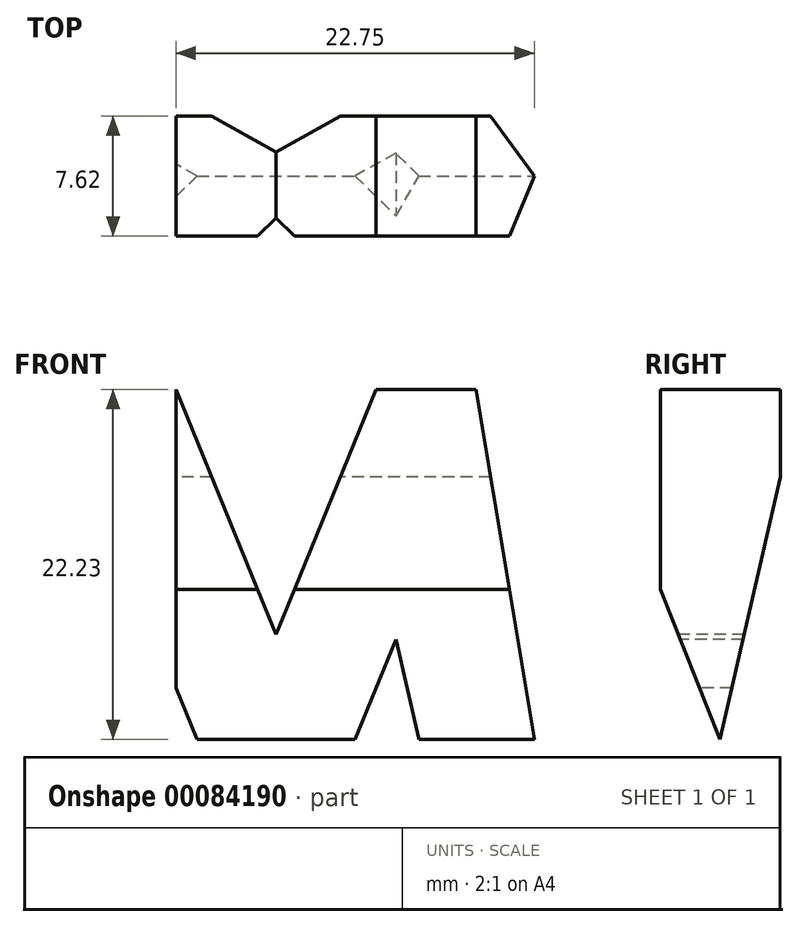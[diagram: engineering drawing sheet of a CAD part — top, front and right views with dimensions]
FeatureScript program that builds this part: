
annotation { "Feature Type Name" : "Feature", "Feature Type Description" : "" }
export const myFeature = defineFeature(function(context is Context, id is Id, definition is map)
    precondition{}
    {
        {
            var Q0;
            Q0=qCreatedBy(makeId("Front.planeOp"),FACE);
            var sketch = newSketch(context, id + "F0", { "sketchPlane" : qUnion([Q0])});
            skLineSegment(sketch, "E0", {"start": v(0, 0) * mm, "end": v(0, 38.1) * mm});
            skLineSegment(sketch, "E1", {"start": v(0, 38.1) * mm, "end": v(38.1, 38.1) * mm});
            skLineSegment(sketch, "E2", {"start": v(38.1, 38.1) * mm, "end": v(38.1, 0) * mm});
            skLineSegment(sketch, "E3", {"start": v(0, 0) * mm, "end": v(38.1, 0) * mm});
            skSolve(sketch);
        }
        {
            var Q0;
            Q0=makeQuery(id+"F0.imprint","IMPRINT",FACE,{"disambiguationData":[TD([[makeQuery(id+"F0.imprint","IMPRINT",EDGE,{"derivedFrom":sQuery(id+"F0.wireOp",EDGE,"E0")}),-1.0]])]});
            extrude(context, id + "F1", {"entities" : qUnion([Q0]), "depth" : 38.1 * mm});
        }
        {
            var Q0;
            Q0=qCreatedBy(makeId("Front.planeOp"),FACE);
            cPlane(context, id + "F2", {"entities" : qUnion([Q0]), "cplaneType" : CPlaneType.OFFSET, "offset" : 38.1 * mm, "width" : 152.4 * mm, "height" : 152.4 * mm});
        }
        {
            var Q0;
            Q0=qCreatedBy(makeId("Right.planeOp"),FACE);
            cPlane(context, id + "F3", {"entities" : qUnion([Q0]), "cplaneType" : CPlaneType.OFFSET, "offset" : 38.1 * mm, "width" : 152.4 * mm, "height" : 152.4 * mm});
        }
        {
            var Q0;
            Q0=qCreatedBy(makeId("Top.planeOp"),FACE);
            cPlane(context, id + "F4", {"entities" : qUnion([Q0]), "cplaneType" : CPlaneType.OFFSET, "offset" : 38.1 * mm, "width" : 152.4 * mm, "height" : 152.4 * mm});
        }
        {
            var Q0;
            Q0=qCreatedBy(id+"F3.planeOp",FACE);
            var sketch = newSketch(context, id + "F5", { "sketchPlane" : qUnion([Q0])});
            skLineSegment(sketch, "E4", {"start": v(0, 0) * mm, "end": v(-38.1, 0) * mm});
            skLineSegment(sketch, "E5", {"start": v(-38.1, 0) * mm, "end": v(-38.1, 38.1) * mm});
            skLineSegment(sketch, "E6", {"start": v(-38.1, 38.1) * mm, "end": v(0, 38.1) * mm});
            skLineSegment(sketch, "E7", {"start": v(0, 38.1) * mm, "end": v(0, -1.8) * mm});
            skLineSegment(sketch, "E8", {"start": v(-38.1, 38.1) * mm, "end": v(-31.75, 0) * mm});
            skLineSegment(sketch, "E9", {"start": v(-31.75, 0) * mm, "end": v(-25.4, 0) * mm});
            skLineSegment(sketch, "E10", {"start": v(-25.4, 0) * mm, "end": v(-19.05, 15.88) * mm});
            skLineSegment(sketch, "E11", {"start": v(-19.05, 15.88) * mm, "end": v(-19.05, 15.88) * mm});
            skLineSegment(sketch, "E12", {"start": v(-19.05, 15.88) * mm, "end": v(-12.7, 0) * mm});
            skLineSegment(sketch, "E13", {"start": v(-12.7, 0) * mm, "end": v(-6.35, 0) * mm});
            skLineSegment(sketch, "E14", {"start": v(-6.35, 0) * mm, "end": v(0, 38.1) * mm});
            skLineSegment(sketch, "E15", {"start": v(-38.1, 38.1) * mm, "end": v(-31.75, 38.1) * mm});
            skLineSegment(sketch, "E16", {"start": v(-31.75, 38.1) * mm, "end": v(-26.67, 15.88) * mm});
            skLineSegment(sketch, "E17", {"start": v(-26.67, 15.88) * mm, "end": v(-21.59, 28.58) * mm});
            skLineSegment(sketch, "E18", {"start": v(-21.59, 28.58) * mm, "end": v(-16.5, 28.58) * mm});
            skLineSegment(sketch, "E19", {"start": v(-16.5, 28.58) * mm, "end": v(-11.43, 15.88) * mm});
            skLineSegment(sketch, "E20", {"start": v(-11.43, 15.87) * mm, "end": v(-6.35, 38.1) * mm});
            skLineSegment(sketch, "E21", {"start": v(-6.35, 38.1) * mm, "end": v(0, 38.1) * mm});
            skSolve(sketch);
        }
        {
            var Q0;
            Q0=makeQuery(id+"F5.imprint","IMPRINT",FACE,{"disambiguationData":[TD([[makeQuery(id+"F5.imprint","IMPRINT",EDGE,{"derivedFrom":sQuery(id+"F5.wireOp",EDGE,"E6")}),-1.0]])]});
            var Q1;
            {var subQ0=sQuery(id+"F5.wireOp",EDGE,"E5");Q1=makeQuery(id+"F5.imprint","IMPRINT",FACE,{"disambiguationData":[TD([[makeQuery(id+"F5.imprint","IMPRINT",EDGE,{"derivedFrom":subQ0}),-1.0]])]});}
            var Q2;
            {var subQ0=sQuery(id+"F5.wireOp",EDGE,"E10");Q2=makeQuery(id+"F5.imprint","IMPRINT",FACE,{"disambiguationData":[TD([[makeQuery(id+"F5.imprint","IMPRINT",EDGE,{"derivedFrom":subQ0}),-1.0]])]});}
            var Q3;
            {var subQ3=sQuery(id+"F5.wireOp",EDGE,"E14");Q3=makeQuery(id+"F5.imprint","IMPRINT",FACE,{"disambiguationData":[TD([[makeQuery(id+"F5.imprint","IMPRINT",EDGE,{"derivedFrom":subQ3}),-1.0]])]});}
            extrude(context, id + "F6", {"entities" : qUnion([Q0, Q1, Q2, Q3]), "operationType" : NewBodyOperationType.REMOVE, "oppositeDirection" : true, "depth" : 38.1 * mm});
        }
        {
            var Q0;
            Q0=qCreatedBy(id+"F2.planeOp",FACE);
            var sketch = newSketch(context, id + "F7", { "sketchPlane" : qUnion([Q0])});
            skLineSegment(sketch, "E22", {"start": v(0, 0) * mm, "end": v(0, 38.1) * mm});
            skLineSegment(sketch, "E23", {"start": v(0, 38.1) * mm, "end": v(38.1, 38.1) * mm});
            skLineSegment(sketch, "E24", {"start": v(38.1, 38.1) * mm, "end": v(38.1, 0) * mm});
            skLineSegment(sketch, "E25", {"start": v(0, 0) * mm, "end": v(38.1, 0) * mm});
            skLineSegment(sketch, "E26", {"start": v(0, 0) * mm, "end": v(6.35, 38.1) * mm});
            skLineSegment(sketch, "E27", {"start": v(6.35, 38.1) * mm, "end": v(12.7, 38.1) * mm});
            skLineSegment(sketch, "E28", {"start": v(12.7, 38.1) * mm, "end": v(19.05, 22.56) * mm});
            skLineSegment(sketch, "E29", {"start": v(19.05, 22.56) * mm, "end": v(25.4, 38.1) * mm});
            skLineSegment(sketch, "E30", {"start": v(25.4, 38.1) * mm, "end": v(31.75, 38.1) * mm});
            skLineSegment(sketch, "E31", {"start": v(31.75, 38.1) * mm, "end": v(38.1, 0) * mm});
            skLineSegment(sketch, "E32", {"start": v(0, 0) * mm, "end": v(6.35, 0) * mm});
            skLineSegment(sketch, "E33", {"start": v(6.35, 0) * mm, "end": v(11.43, 22.23) * mm});
            skLineSegment(sketch, "E34", {"start": v(11.43, 22.22) * mm, "end": v(16.51, 9.86) * mm});
            skLineSegment(sketch, "E35", {"start": v(16.51, 9.86) * mm, "end": v(21.59, 9.86) * mm});
            skLineSegment(sketch, "E36", {"start": v(21.59, 9.86) * mm, "end": v(26.67, 22.22) * mm});
            skLineSegment(sketch, "E37", {"start": v(26.67, 22.22) * mm, "end": v(31.75, 0) * mm});
            skSolve(sketch);
        }
        {
            var Q0;
            {var subQ0=sQuery(id+"F7.wireOp",EDGE,"E22");Q0=makeQuery(id+"F7.imprint","IMPRINT",FACE,{"disambiguationData":[TD([[makeQuery(id+"F7.imprint","IMPRINT",EDGE,{"derivedFrom":subQ0}),-1.0]])]});}
            var Q1;
            {var subQ0=sQuery(id+"F7.wireOp",EDGE,"E28");Q1=makeQuery(id+"F7.imprint","IMPRINT",FACE,{"disambiguationData":[TD([[makeQuery(id+"F7.imprint","IMPRINT",EDGE,{"derivedFrom":subQ0}),1.0]])]});}
            var Q2;
            {var subQ0=sQuery(id+"F7.wireOp",EDGE,"E24");Q2=makeQuery(id+"F7.imprint","IMPRINT",FACE,{"disambiguationData":[TD([[makeQuery(id+"F7.imprint","IMPRINT",EDGE,{"derivedFrom":subQ0}),-1.0]])]});}
            var Q3;
            {var subQ0=sQuery(id+"F7.wireOp",EDGE,"E33");Q3=makeQuery(id+"F7.imprint","IMPRINT",FACE,{"disambiguationData":[TD([[makeQuery(id+"F7.imprint","IMPRINT",EDGE,{"derivedFrom":subQ0}),-1.0]])]});}
            extrude(context, id + "F8", {"entities" : qUnion([Q0, Q1, Q2, Q3]), "operationType" : NewBodyOperationType.REMOVE, "oppositeDirection" : true, "depth" : 38.1 * mm});
        }
        {
            var Q0;
            Q0=qCreatedBy(id+"F4.planeOp",FACE);
            var sketch = newSketch(context, id + "F9", { "sketchPlane" : qUnion([Q0])});
            skLineSegment(sketch, "E38", {"start": v(0, 0) * mm, "end": v(38.1, 0) * mm});
            skLineSegment(sketch, "E39", {"start": v(38.1, 0) * mm, "end": v(38.1, -38.1) * mm});
            skLineSegment(sketch, "E40", {"start": v(38.1, -38.1) * mm, "end": v(0, -38.1) * mm});
            skLineSegment(sketch, "E41", {"start": v(0, -38.1) * mm, "end": v(0, 0) * mm});
            skLineSegment(sketch, "E42", {"start": v(38.1, 0) * mm, "end": v(0, 0) * mm});
            skLineSegment(sketch, "E43", {"start": v(0, 0) * mm, "end": v(0, -16.52) * mm});
            skLineSegment(sketch, "E44", {"start": v(-0.1, -22.86) * mm, "end": v(25.4, -22.86) * mm});
            skLineSegment(sketch, "E45", {"start": v(25.4, -22.86) * mm, "end": v(25.4, -30.48) * mm});
            skLineSegment(sketch, "E46", {"start": v(25.4, -30.48) * mm, "end": v(0, -30.48) * mm});
            skLineSegment(sketch, "E47", {"start": v(0, -30.48) * mm, "end": v(0, -38.1) * mm});
            skLineSegment(sketch, "E48", {"start": v(0, -38.1) * mm, "end": v(38.1, -38.1) * mm});
            skLineSegment(sketch, "E49", {"start": v(38.1, -38.1) * mm, "end": v(38.1, -15.24) * mm});
            skLineSegment(sketch, "E50", {"start": v(38.1, -15.24) * mm, "end": v(12.7, -15.24) * mm});
            skLineSegment(sketch, "E51", {"start": v(12.7, -15.24) * mm, "end": v(12.7, -7.62) * mm});
            skLineSegment(sketch, "E52", {"start": v(12.7, -7.62) * mm, "end": v(38.1, -7.62) * mm});
            skLineSegment(sketch, "E53", {"start": v(38.1, -7.62) * mm, "end": v(38.1, 0) * mm});
            skSolve(sketch);
        }
        {
            var Q0;
            Q0=makeQuery(id+"F9.imprint","IMPRINT",FACE,{"disambiguationData":[TD([[makeQuery(id+"F9.imprint","IMPRINT",EDGE,{"derivedFrom":sQuery(id+"F9.wireOp",EDGE,"E39")}),-1.0]])]});
            var Q1;
            {var subQ4=sQuery(id+"F9.wireOp",EDGE,"E45");Q1=makeQuery(id+"F9.imprint","IMPRINT",FACE,{"disambiguationData":[TD([[makeQuery(id+"F9.imprint","IMPRINT",EDGE,{"derivedFrom":subQ4}),-1.0]])]});}
            extrude(context, id + "F10", {"entities" : qUnion([Q0, Q1]), "operationType" : NewBodyOperationType.REMOVE, "oppositeDirection" : true, "depth" : 38.1 * mm});
        }
    });
